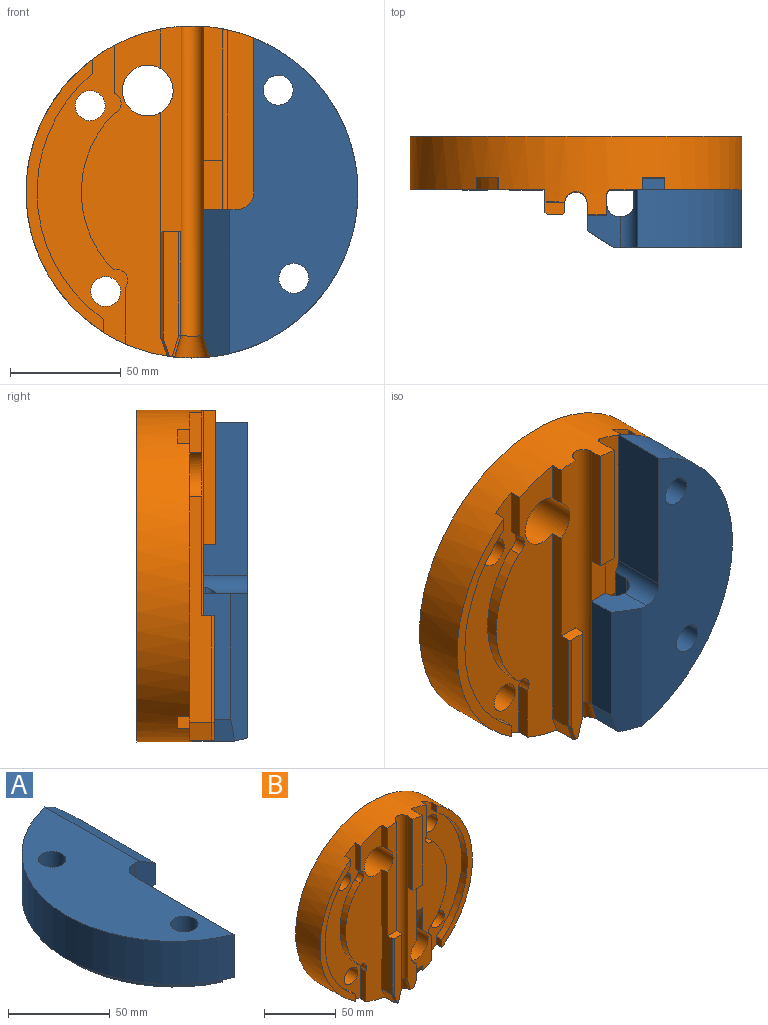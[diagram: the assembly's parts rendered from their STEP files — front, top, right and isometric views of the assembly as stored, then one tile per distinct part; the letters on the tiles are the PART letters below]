
ASSEMBLY  parts=2 mates=1
PART A: 28 faces, bbox 70x144.2x31 mm
  f0: plane 139.93x49mm, normal (0,0,-1), area 2400.9mm2, adj f1,f2,f11,f12,f13,f17,f18,f19
  f1: plane 14.71x7mm, normal (1,0,0), area 103mm2, adj f0,f3,f11,f24
  f2: plane 30.72x7mm, normal (1,0,0), area 215.1mm2, adj f0,f4,f13,f24
  f3: cylinder r=5mm len=16.36mm, axis (0,1,0), area 114.4mm2, adj f1,f11,f22,f24
  f4: cylinder r=5mm len=30.72mm, axis (0,1,0), area 225.1mm2, adj f2,f13,f22,f24
  f5: plane 18.05x1mm, normal (-1,0,0), area 18mm2, adj f7,f11,f23,f26
  f6: plane 28.02x1mm, normal (-1,0,0), area 28mm2, adj f8,f9,f23,f26
  f7: cylinder r=5mm len=18.05mm, axis (0,1,0), area 132.6mm2, adj f5,f11,f22,f23
  f8: cylinder r=5mm len=28.02mm, axis (0,1,0), area 213.9mm2, adj f6,f9,f22,f23
  f9: plane 20x15mm, normal (0,-1,0), area 224.4mm2, adj f6,f8,f10,f13,f16,f22,f25,f26
  f10: plane 56.79x12.5mm, normal (1,0,0), area 709.8mm2, adj f9,f25,f26,f27
  f11: cylinder r=75mm len=144.16mm, axis (0,0,-1), area 4972.9mm2, adj f0,f1,f3,f5,f7,f12,f16,f22
  f12: plane 69.58x26mm, normal (1,0,0), area 1809mm2, adj f0,f11,f13,f16
  f13: cylinder r=8mm len=26mm, axis (0,0,-1), area 252.3mm2, adj f0,f2,f4,f9,f12,f16,f22
  f14: cylinder r=6.75mm len=31mm, axis (0,0,-1), area 1314.8mm2, adj f16,f21
  f15: cylinder r=6.75mm len=31mm, axis (0,0,-1), area 1314.8mm2, adj f16,f21
  f16: plane 142.63x58mm, normal (0,0,1), area 5161mm2, adj f9,f11,f12,f13,f14,f15,f25
  f17: cylinder r=70mm len=123.87mm, axis (0,0,1), area 761.3mm2, adj f0,f18,f20,f21
  f18: plane 24.91x5mm, normal (1,0,0), area 124.6mm2, adj f0,f17,f19,f21
  f19: cylinder r=50mm len=75.71mm, axis (0,0,1), area 430.7mm2, adj f0,f18,f20,f21
  f20: plane 23.25x5mm, normal (1,0,0), area 116.2mm2, adj f0,f17,f19,f21
  f21: plane 123.87x40mm, normal (0,0,-1), area 2104.6mm2, adj f14,f15,f17,f18,f19,f20
  f22: plane 64.62x23mm, normal (0,0,-1), area 498.1mm2, adj f3,f4,f7,f8,f9,f11,f13,f23
  f23: cylinder r=11.5mm len=22.91mm, axis (0,0,-1), area 152.9mm2, adj f5,f6,f7,f8,f22,f26
  f24: cylinder r=11.5mm len=22.91mm, axis (0,0,-1), area 294mm2, adj f0,f1,f2,f3,f4,f22
  f25: plane 66.62x12.03mm, normal (0.53,0,0.85), area 918.4mm2, adj f9,f10,f11,f16,f27
  f26: plane 66.59x9mm, normal (0,0,-1), area 506.4mm2, adj f5,f6,f9,f10,f11,f23,f27
  f27: plane 14.3x9.8mm, normal (0.96,0.28,0), area 136.8mm2, adj f10,f11,f25,f26
PART B: 56 faces, bbox 152.5x38x152.6 mm
  f0: cylinder r=75mm len=150mm, axis (0,1,0), area 11260mm2, adj f1,f3,f5,f7,f8,f9,f10,f11
  f1: plane 143.62x36mm, normal (0,-1,0), area 2710.6mm2, adj f0,f2,f6,f27,f28,f29,f30,f31
  f2: cylinder r=11.5mm len=30mm, axis (0,1,0), area 1792.1mm2, adj f1,f5,f6,f10,f11,f46,f47
  f3: plane 18.05x5.5mm, normal (-1,0,0), area 99.2mm2, adj f0,f8,f33,f38
  f4: plane 102.15x10mm, normal (-1,0,0), area 778.4mm2, adj f8,f33,f34,f38,f41,f43
  f5: plane 109.7x18.08mm, normal (1,0,0), area 873mm2, adj f0,f2,f11,f35,f37,f46,f51
  f6: plane 13x6.98mm, normal (1,0,0), area 79.2mm2, adj f1,f2,f11,f48,f50
  f7: plane 123.44x35mm, normal (0,-1,0), area 684.2mm2, adj f0,f24,f25,f26
  f8: plane 147.83x38.75mm, normal (0,-1,0), area 3190.4mm2, adj f0,f3,f4,f18,f19,f20,f21,f22
  f9: plane 56.47x7mm, normal (0,-1,0), area 368.6mm2, adj f0,f34,f42,f43,f44,f45
  f10: plane 150x150mm, normal (0,1,0), area 16268mm2, adj f0,f2,f38,f52,f53,f54,f55
  f11: plane 88.84x9mm, normal (0,-1,0), area 700mm2, adj f0,f2,f5,f6,f12,f35,f40,f50
  f12: cylinder r=5mm len=140.15mm, axis (0,0,1), area 2150.8mm2, adj f0,f11,f13,f33,f34,f36,f40
  f13: plane 46.79x4mm, normal (1,0,0), area 187.1mm2, adj f12,f34,f39,f45
  f14: plane 123.44x35mm, normal (0,-1,0), area 684.2mm2, adj f0,f15,f16,f17
  f15: plane 6.38x5.5mm, normal (1,0,0), area 35.1mm2, adj f0,f14,f16,f23
  f16: cylinder r=70mm len=111.06mm, axis (0,-1,0), area 706.5mm2, adj f14,f15,f17,f23
  f17: plane 6x5.5mm, normal (1,0,0), area 33mm2, adj f0,f14,f16,f23
  f18: plane 25.74x5.5mm, normal (-1,0,0), area 141.6mm2, adj f0,f8,f19,f23
  f19: cylinder r=5mm len=8mm, axis (0,-1,0), area 69.2mm2, adj f8,f18,f20,f23
  f20: cylinder r=50mm len=70.47mm, axis (0,-1,0), area 430.1mm2, adj f8,f19,f21,f23
  f21: cylinder r=5mm len=9.34mm, axis (0,-1,0), area 66.5mm2, adj f8,f20,f22,f23
  f22: plane 21.75x5.5mm, normal (-1,0,0), area 119.6mm2, adj f0,f8,f21,f23
  f23: plane 135.07x41mm, normal (0,-1,0), area 2258.4mm2, adj f0,f15,f16,f17,f18,f19,f20,f21
  f24: plane 6.38x5.5mm, normal (-1,0,0), area 35.1mm2, adj f0,f7,f25,f32
  f25: cylinder r=70mm len=111.06mm, axis (0,-1,0), area 706.5mm2, adj f7,f24,f26,f32
  f26: plane 6x5.5mm, normal (-1,0,0), area 33mm2, adj f0,f7,f25,f32
  f27: plane 25.74x5.5mm, normal (1,0,0), area 141.6mm2, adj f0,f1,f28,f32
  f28: cylinder r=5mm len=8mm, axis (0,-1,0), area 69.2mm2, adj f1,f27,f29,f32
  f29: cylinder r=50mm len=70.47mm, axis (0,-1,0), area 430.1mm2, adj f1,f28,f30,f32
  f30: cylinder r=5mm len=9.34mm, axis (0,-1,0), area 66.5mm2, adj f1,f29,f31,f32
  f31: plane 21.75x5.5mm, normal (1,0,0), area 119.6mm2, adj f0,f1,f30,f32
  f32: plane 135.07x41mm, normal (0,-1,0), area 2258.4mm2, adj f0,f24,f25,f26,f27,f28,f29,f30
  f33: plane 92.84x9.03mm, normal (0,-1,0), area 757.2mm2, adj f0,f3,f4,f12,f34,f38
  f34: plane 9.03x5.5mm, normal (0,0,1), area 48.5mm2, adj f4,f9,f12,f13,f33,f43,f45
  f35: plane 9x5.5mm, normal (0,0,-1), area 49.5mm2, adj f5,f11,f36,f37
  f36: plane 60.58x5.5mm, normal (-1,0,0), area 333.2mm2, adj f0,f12,f35,f37
  f37: plane 60.58x9mm, normal (0,-1,0), area 540.9mm2, adj f0,f5,f35,f36
  f38: cylinder r=11.5mm len=29.5mm, axis (0,1,0), area 1863.4mm2, adj f3,f4,f8,f10,f33
  f39: plane 9.8x4mm, normal (0.96,0,-0.28), area 40.9mm2, adj f0,f13,f40,f44
  f40: bspline ~15.87x10.32mm, area 196.6mm2, adj f0,f11,f12,f39
  f41: plane 10x8.02mm, normal (-0.95,0,-0.32), area 84.8mm2, adj f0,f4,f8,f42
  f42: plane 8.34x3.87mm, normal (-0.67,-0.71,-0.23), area 12.2mm2, adj f0,f9,f41,f43
  f43: plane 48.13x1mm, normal (-0.71,-0.71,0), area 68mm2, adj f4,f9,f34,f42
  f44: plane 9.94x3.88mm, normal (0.68,-0.71,-0.2), area 14.5mm2, adj f0,f9,f39,f45
  f45: plane 46.79x1mm, normal (0.71,-0.71,0), area 66.1mm2, adj f9,f13,f34,f44
  f46: plane 27.48x14.45mm, normal (0,-0.95,-0.32), area 231.6mm2, adj f1,f2,f5,f47,f51
  f47: plane 19.19x6.58mm, normal (-1,0,0), area 63.1mm2, adj f1,f2,f46
  f48: plane 14.65x7.96mm, normal (0,-0.93,-0.37), area 84.9mm2, adj f0,f1,f6,f49,f50
  f49: plane 4.17x1.66mm, normal (-1,0,0), area 3.5mm2, adj f0,f1,f48
  f50: plane 9.17x5.5mm, normal (0.9,0,-0.43), area 49.3mm2, adj f0,f6,f11,f48
  f51: cylinder r=2mm len=90.51mm, axis (0,0,1), area 274.5mm2, adj f0,f1,f5,f46
  f52: cylinder r=6.75mm len=18.5mm, axis (0,-1,0), area 784.6mm2, adj f10,f32
  f53: cylinder r=6.75mm len=18.5mm, axis (0,-1,0), area 784.6mm2, adj f10,f32
  f54: cylinder r=6.75mm len=18.5mm, axis (0,-1,0), area 784.6mm2, adj f10,f23
  f55: cylinder r=6.75mm len=18.5mm, axis (0,-1,0), area 784.6mm2, adj f10,f23
PLACE A rot(axis=(0,-0.71,0.71),180deg) t=(0,-24,0)mm
PLACE B at identity fixed
MATE fastened A.f14 <-> B.f52  axis (0,1,0) through (39,-19,46)mm
